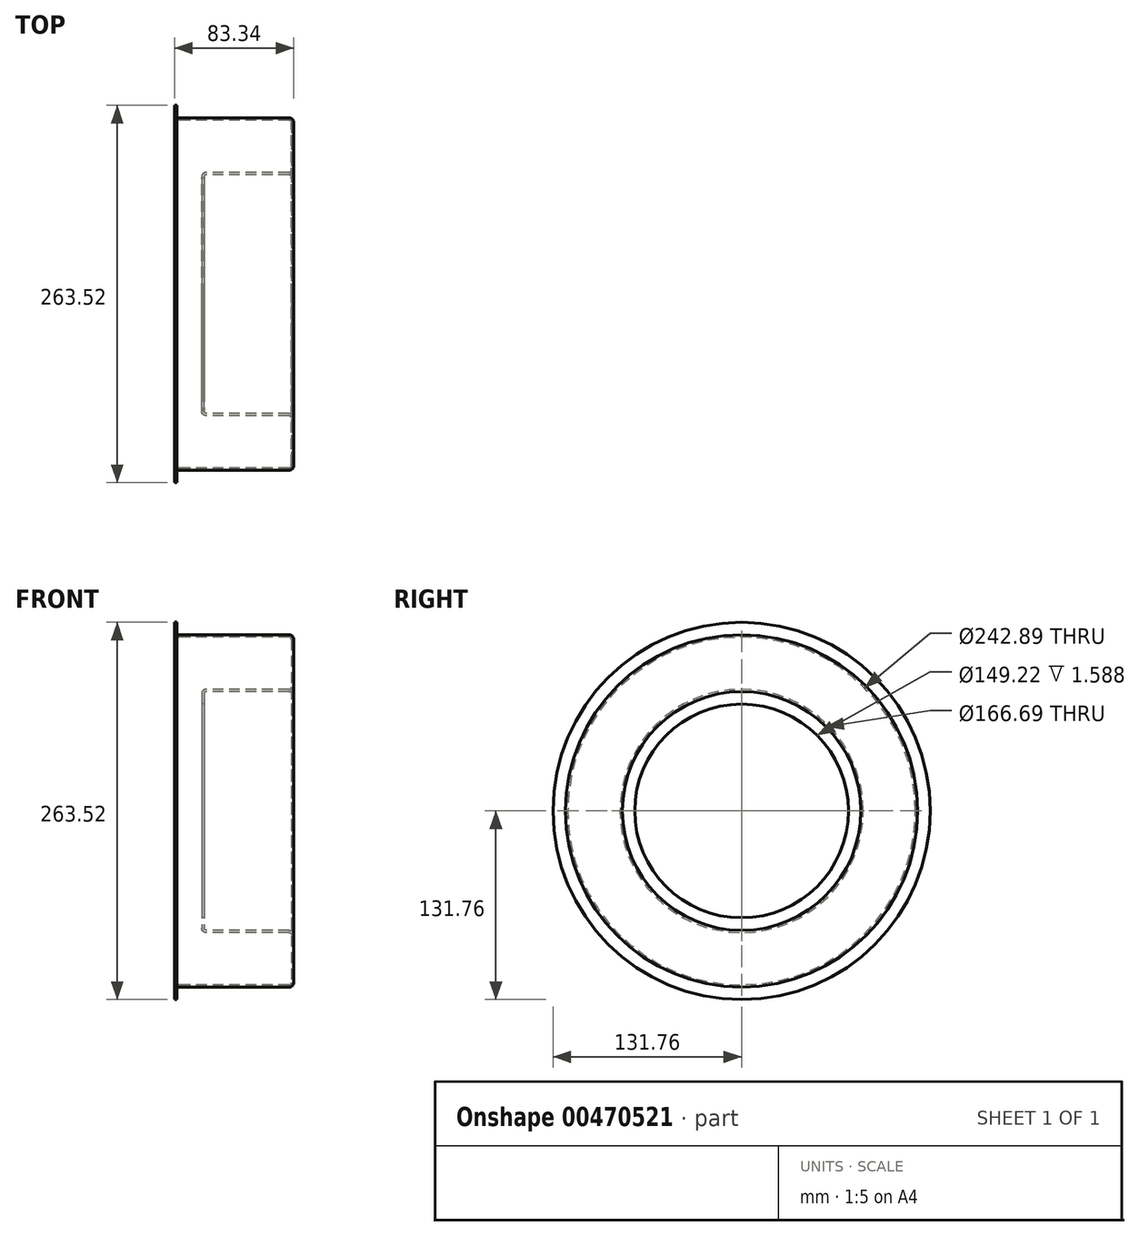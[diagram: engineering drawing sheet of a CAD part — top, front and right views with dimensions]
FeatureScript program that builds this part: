
annotation { "Feature Type Name" : "Feature", "Feature Type Description" : "" }
export const myFeature = defineFeature(function(context is Context, id is Id, definition is map)
    precondition{}
    {
        {
            var Q0;
            Q0=qCreatedBy(makeId("Top.planeOp"),FACE);
            var sketch = newSketch(context, id + "F0", { "sketchPlane" : qUnion([Q0])});
            skLineSegment(sketch, "E0", {"start": v(19.05, 74.61) * mm, "end": v(20.64, 74.61) * mm});
            skLineSegment(sketch, "E1", {"start": v(20.64, 74.61) * mm, "end": v(20.64, 81.76) * mm});
            skLineSegment(sketch, "E2", {"start": v(22.22, 83.34) * mm, "end": v(80.17, 83.34) * mm});
            skLineSegment(sketch, "E3", {"start": v(83.34, 86.52) * mm, "end": v(83.34, 119.86) * mm});
            skLineSegment(sketch, "E4", {"start": v(80.17, 123.03) * mm, "end": v(3.18, 123.03) * mm});
            skLineSegment(sketch, "E5", {"start": v(1.59, 124.62) * mm, "end": v(1.59, 131.76) * mm});
            skLineSegment(sketch, "E6", {"start": v(1.59, 131.76) * mm, "end": v(0, 131.76) * mm});
            skLineSegment(sketch, "E7", {"start": v(0, 131.76) * mm, "end": v(0, 124.62) * mm});
            skLineSegment(sketch, "E8", {"start": v(3.18, 121.44) * mm, "end": v(80.17, 121.44) * mm});
            skLineSegment(sketch, "E9", {"start": v(81.76, 119.86) * mm, "end": v(81.76, 86.52) * mm});
            skLineSegment(sketch, "E10", {"start": v(80.17, 84.93) * mm, "end": v(22.22, 84.93) * mm});
            skLineSegment(sketch, "E11", {"start": v(19.05, 81.76) * mm, "end": v(19.05, 74.61) * mm});
            skPoint(sketch, "E12.visualSharp", {"position": v(20.64, 83.34) * mm});
            skArc(sketch, "E12.filletArc", {"start": v(22.22, 83.34) * mm, "mid": v(21.1, 82.88) * mm, "end": v(20.64, 81.76) * mm});
            skPoint(sketch, "E13.visualSharp", {"position": v(81.76, 84.93) * mm});
            skArc(sketch, "E13.filletArc", {"start": v(80.17, 84.93) * mm, "mid": v(81.3, 85.4) * mm, "end": v(81.76, 86.52) * mm});
            skPoint(sketch, "E14.visualSharp", {"position": v(81.76, 121.44) * mm});
            skArc(sketch, "E14.filletArc", {"start": v(81.76, 119.86) * mm, "mid": v(81.3, 120.98) * mm, "end": v(80.17, 121.44) * mm});
            skPoint(sketch, "E15.visualSharp", {"position": v(1.59, 123.03) * mm});
            skArc(sketch, "E15.filletArc", {"start": v(1.59, 124.62) * mm, "mid": v(2.05, 123.5) * mm, "end": v(3.18, 123.03) * mm});
            skPoint(sketch, "E16.visualSharp", {"position": v(0, 121.44) * mm});
            skArc(sketch, "E16.filletArc", {"start": v(0, 124.62) * mm, "mid": v(0.93, 122.37) * mm, "end": v(3.18, 121.44) * mm});
            skPoint(sketch, "E17.visualSharp", {"position": v(83.34, 123.03) * mm});
            skArc(sketch, "E17.filletArc", {"start": v(83.34, 119.86) * mm, "mid": v(82.41, 122.1) * mm, "end": v(80.17, 123.03) * mm});
            skPoint(sketch, "E18.visualSharp", {"position": v(83.34, 83.34) * mm});
            skArc(sketch, "E18.filletArc", {"start": v(80.17, 83.34) * mm, "mid": v(82.41, 84.27) * mm, "end": v(83.34, 86.52) * mm});
            skPoint(sketch, "E19.visualSharp", {"position": v(19.05, 84.93) * mm});
            skArc(sketch, "E19.filletArc", {"start": v(22.22, 84.93) * mm, "mid": v(19.98, 84) * mm, "end": v(19.05, 81.76) * mm});
            skLineSegment(sketch, "E20", {"start": v(0, 0) * mm, "end": v(133.91, 0) * mm});
            skSolve(sketch);
        }
        {
            var Q0;
            Q0=makeQuery(id+"F0.imprint","IMPRINT",FACE,{"disambiguationData":[TD([[makeQuery(id+"F0.imprint","IMPRINT",EDGE,{"derivedFrom":sQuery(id+"F0.wireOp",EDGE,"E0")}),1.0]])]});
            var Q1;
            Q1=sQuery(id+"F0.wireOp",EDGE,"E20");
            revolve(context, id + "F1", {"entities" : qUnion([Q0]), "axis" : qUnion([Q1]), "revolveType" : RevolveType.FULL});
        }
    });
